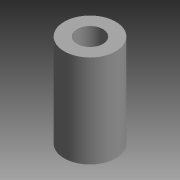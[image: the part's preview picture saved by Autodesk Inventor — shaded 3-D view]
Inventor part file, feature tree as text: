
AUTODESK INVENTOR PART (.ipt)
format: ipt  version: 2015 (Build 190159000, 159)  size: 74,240 bytes
history: native  units: mm
features: sketch x1, plane x1, extrude x1, reference x1
ambient origin geometry x8: Origin, YZ Plane, XZ Plane, XY Plane, X Axis, Y Axis, Z Axis, Center Point
bodies: Solid1 (feature_tree)
feature tree (4):
  sketch  "Sketch1"  dims[d0=5.0mm d1=10.0mm d2=10.0mm d3=0.0mm]
  plane  "Work Plane1"
  extrude  "Extrusion1"  Depth=10.0mm
  reference  "Reference1"
